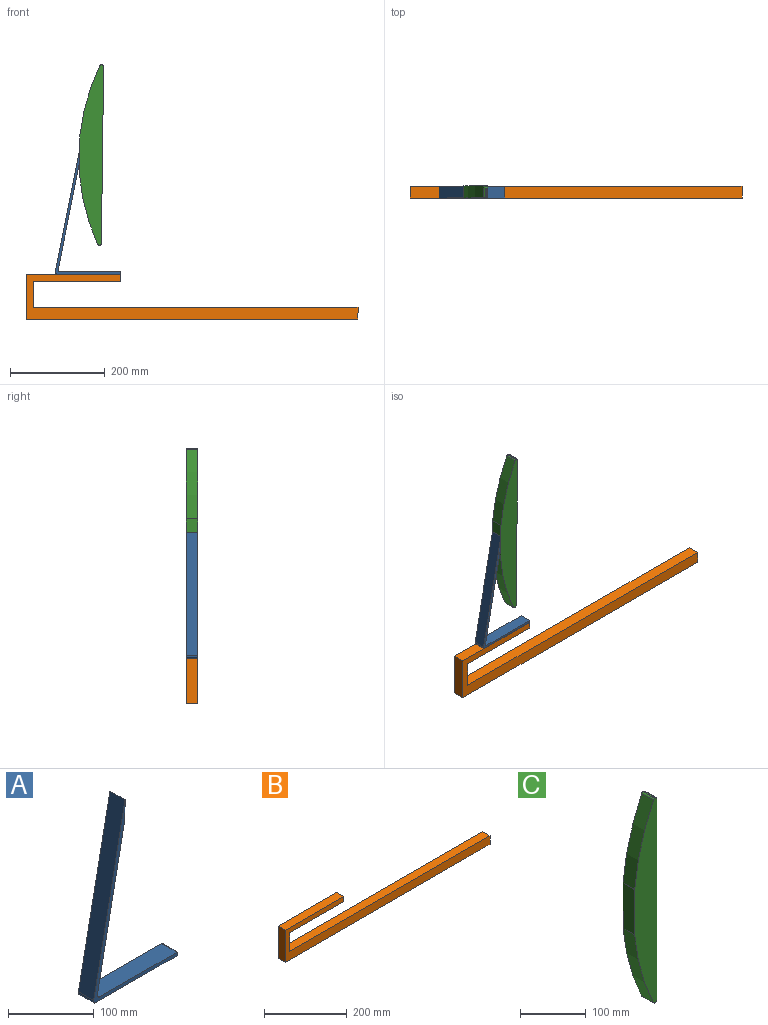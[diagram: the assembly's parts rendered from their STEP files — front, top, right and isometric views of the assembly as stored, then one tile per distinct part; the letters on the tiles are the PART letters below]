
ASSEMBLY  parts=3 mates=2
PART A: 12 faces, bbox 138.5x25x265 mm
  f0: plane 25x3mm, normal (1,0,0), area 75mm2, adj f8,f9,f10,f11
  f1: plane 127.07x25mm, normal (0,0,1), area 3176.8mm2, adj f2,f8,f9,f10
  f2: cylinder r=4.1mm len=25mm, axis (0,1,0), area 181.3mm2, adj f1,f3,f8,f9
  f3: plane 227.69x45.22mm, normal (0.98,0,-0.19), area 5803.4mm2, adj f2,f4,f8,f9
  f4: plane 27.41x25mm, normal (1,0,-0.01), area 685.3mm2, adj f3,f5,f8,f9
  f5: plane 260.32x51.7mm, normal (-0.98,0,0.19), area 6635.2mm2, adj f4,f6,f8,f9
  f6: cylinder r=3.46mm len=25mm, axis (0,1,0), area 167mm2, adj f5,f7,f8,f9
  f7: plane 134x25mm, normal (0,0,-1), area 3350mm2, adj f6,f8,f9,f11
  f8: plane 265x138.46mm, normal (0,-1,0), area 1950.3mm2, adj f0,f1,f2,f3,f4,f5,f6,f7
  f9: plane 265x138.46mm, normal (0,1,0), area 1950.3mm2, adj f0,f1,f2,f3,f4,f5,f6,f7
  f10: cylinder r=1mm len=25mm, axis (0,-1,0), area 39.3mm2, adj f0,f1,f8,f9
  f11: cylinder r=1mm len=25mm, axis (0,1,0), area 39.3mm2, adj f0,f7,f8,f9
PART B: 10 faces, bbox 700x25x95 mm
  f0: plane 700x25mm, normal (0,0,-1), area 17500mm2, adj f1,f7,f8,f9
  f1: plane 25x25mm, normal (1,0,0), area 625mm2, adj f0,f2,f8,f9
  f2: plane 685x25mm, normal (0,0,1), area 17125mm2, adj f1,f3,f8,f9
  f3: plane 55x25mm, normal (1,0,0), area 1375mm2, adj f2,f4,f8,f9
  f4: plane 185x25mm, normal (0,0,-1), area 4625mm2, adj f3,f5,f8,f9
  f5: plane 25x15mm, normal (1,0,0), area 375mm2, adj f4,f6,f8,f9
  f6: plane 200x25mm, normal (0,0,1), area 5000mm2, adj f5,f7,f8,f9
  f7: plane 95x25mm, normal (-1,0,0), area 2375mm2, adj f0,f6,f8,f9
  f8: plane 700x95mm, normal (0,-1,0), area 21325mm2, adj f0,f1,f2,f3,f4,f5,f6,f7
  f9: plane 700x95mm, normal (0,1,0), area 21325mm2, adj f0,f1,f2,f3,f4,f5,f6,f7
PART C: 13 faces, bbox 48x25x380 mm
  f0: plane 83.79x25mm, normal (-1,0,0), area 2094.7mm2, adj f1,f6,f7,f12
  f1: cylinder r=441.27mm len=146.32mm, axis (0,1,0), area 3812.3mm2, adj f0,f6,f7,f8
  f2: plane 25x2.1mm, normal (0,0,-1), area 52.6mm2, adj f6,f7,f8,f9
  f3: plane 374x25mm, normal (1,0,0), area 9350mm2, adj f6,f7,f9,f10
  f4: plane 25x2.1mm, normal (0,0,1), area 52.6mm2, adj f6,f7,f10,f11
  f5: cylinder r=441.27mm len=146.17mm, axis (0,1,0), area 3808.7mm2, adj f6,f7,f11,f12
  f6: plane 380x48mm, normal (0,-1,0), area 13547.1mm2, adj f0,f1,f2,f3,f4,f5,f8,f9
  f7: plane 380x48mm, normal (0,1,0), area 13547.1mm2, adj f0,f1,f2,f3,f4,f5,f8,f9
  f8: cylinder r=3mm len=25mm, axis (0,1,0), area 84.7mm2, adj f1,f2,f6,f7
  f9: cylinder r=3mm len=25mm, axis (0,-1,0), area 117.8mm2, adj f2,f3,f6,f7
  f10: cylinder r=3mm len=25mm, axis (0,1,0), area 117.8mm2, adj f3,f4,f6,f7
  f11: cylinder r=3mm len=25mm, axis (0,1,0), area 84.7mm2, adj f4,f5,f6,f7
  f12: cylinder r=3mm len=25mm, axis (0,1,0), area 7.2mm2, adj f0,f5,f6,f7
PLACE A t=(-332.26,-148.59,40.63)mm
PLACE B t=(207.74,-148.59,-54.37)mm
PLACE C rot(axis=(0,1,0),0.7deg) t=(-333.36,-148.59,101.41)mm
MATE parallel C.f0 <-> A.f4  axis (-1,0,0.01) through (-378.96,-161.09,291.92)mm
MATE parallel B.f6 <-> A.f7  axis (0,0,1) through (-392.26,-161.09,40.63)mm
